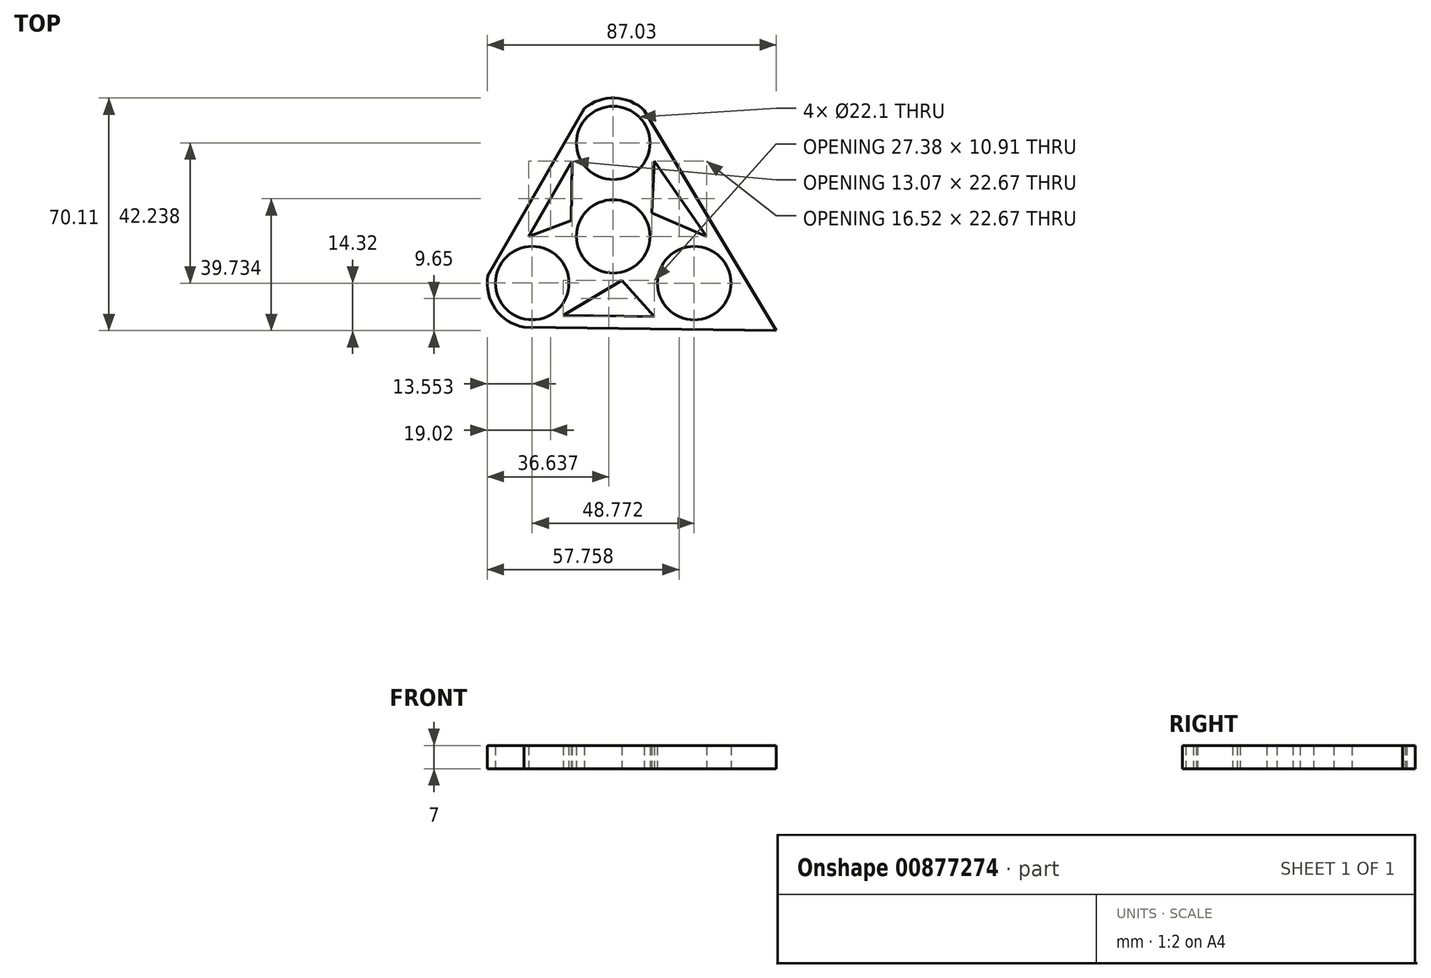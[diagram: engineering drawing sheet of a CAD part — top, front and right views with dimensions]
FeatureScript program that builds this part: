
annotation { "Feature Type Name" : "Feature", "Feature Type Description" : "" }
export const myFeature = defineFeature(function(context is Context, id is Id, definition is map)
    precondition{}
    {
        {
            var Q0;
            Q0=qCreatedBy(makeId("Top.planeOp"),FACE);
            var sketch = newSketch(context, id + "F0", { "sketchPlane" : qUnion([Q0])});
            skCircle(sketch, "E0", {"center": v(0, 0) * mm, "radius": 13.55 * mm});
            skCircle(sketch, "E1", {"center": v(0, 0) * mm, "radius": 11.05 * mm});
            skCircle(sketch, "E2", {"center": v(0, 28.16) * mm, "radius": 13.55 * mm});
            skCircle(sketch, "E3", {"center": v(0, 28.16) * mm, "radius": 11.05 * mm});
            skCircle(sketch, "E4.1.0", {"center": v(-24.39, -14.08) * mm, "radius": 11.05 * mm});
            skCircle(sketch, "E4.1.1", {"center": v(-24.39, -14.08) * mm, "radius": 13.55 * mm});
            skCircle(sketch, "E4.2.0", {"center": v(24.38, -14.08) * mm, "radius": 11.05 * mm});
            skCircle(sketch, "E4.2.1", {"center": v(24.38, -14.08) * mm, "radius": 13.55 * mm});
            skLineSegment(sketch, "E5", {"start": v(0, 0) * mm, "end": v(62.65, -36.25) * mm, "construction": true});
            skLineSegment(sketch, "E6", {"start": v(0, 0) * mm, "end": v(-56.78, -33.1) * mm, "construction": true});
            skLineSegment(sketch, "E7", {"start": v(0, 0) * mm, "end": v(0, 68.38) * mm, "construction": true});
            skLineSegment(sketch, "E8", {"start": v(0, 53.61) * mm, "end": v(49.09, -28.4) * mm});
            skLineSegment(sketch, "E9", {"start": v(49.09, -28.4) * mm, "end": v(-46.55, -27.14) * mm});
            skLineSegment(sketch, "E10", {"start": v(-46.55, -27.14) * mm, "end": v(0, 53.61) * mm});
            skLineSegment(sketch, "E11", {"start": v(12.39, 22.67) * mm, "end": v(28.08, 0) * mm});
            skLineSegment(sketch, "E12", {"start": v(28.08, 0) * mm, "end": v(11.56, 7.07) * mm});
            skLineSegment(sketch, "E13", {"start": v(11.56, 7.07) * mm, "end": v(12.39, 22.67) * mm});
            skLineSegment(sketch, "E14", {"start": v(-15, -23.84) * mm, "end": v(12.39, -24.2) * mm});
            skLineSegment(sketch, "E15", {"start": v(12.39, -24.2) * mm, "end": v(2.6, -13.3) * mm});
            skLineSegment(sketch, "E16", {"start": v(2.6, -13.3) * mm, "end": v(-15, -23.84) * mm});
            skLineSegment(sketch, "E17", {"start": v(-12.39, 22.67) * mm, "end": v(-25.45, 0) * mm});
            skLineSegment(sketch, "E18", {"start": v(-25.45, 0) * mm, "end": v(-12.66, 4.82) * mm});
            skLineSegment(sketch, "E19", {"start": v(-12.66, 4.82) * mm, "end": v(-12.39, 22.67) * mm});
            skSolve(sketch);
        }
        {
            var Q0;
            {var subQ5=sQuery(id+"F0.wireOp",EDGE,"E16");Q0=makeQuery(id+"F0.imprint","IMPRINT",FACE,{"disambiguationData":[TD([[makeQuery(id+"F0.imprint","IMPRINT",EDGE,{"derivedFrom":subQ5}),-1.0]])]});}
            var Q1;
            {var subQ0=sQuery(id+"F0.wireOp",EDGE,"E13");Q1=makeQuery(id+"F0.imprint","IMPRINT",FACE,{"disambiguationData":[TD([[makeQuery(id+"F0.imprint","IMPRINT",EDGE,{"derivedFrom":subQ0}),1.0]])]});}
            var Q2;
            Q2=makeQuery(id+"F0.imprint","IMPRINT",FACE,{"disambiguationData":[TD([[makeQuery(id+"F0.imprint","IMPRINT",EDGE,{"derivedFrom":sQuery(id+"F0.wireOp",EDGE,"E3")}),-1.0]])]});
            var Q3;
            Q3=makeQuery(id+"F0.imprint","IMPRINT",FACE,{"disambiguationData":[TD([[makeQuery(id+"F0.imprint","IMPRINT",EDGE,{"derivedFrom":sQuery(id+"F0.wireOp",EDGE,"E1")}),-1.0]])]});
            var Q4;
            Q4=makeQuery(id+"F0.imprint","IMPRINT",FACE,{"disambiguationData":[TD([[makeQuery(id+"F0.imprint","IMPRINT",EDGE,{"derivedFrom":sQuery(id+"F0.wireOp",EDGE,"E4.2.1")}),-1.0]])]});
            var Q5;
            Q5=makeQuery(id+"F0.imprint","IMPRINT",FACE,{"disambiguationData":[TD([[makeQuery(id+"F0.imprint","IMPRINT",EDGE,{"derivedFrom":sQuery(id+"F0.wireOp",EDGE,"E4.2.0")}),-1.0]])]});
            var Q6;
            Q6=makeQuery(id+"F0.imprint","IMPRINT",FACE,{"disambiguationData":[TD([[makeQuery(id+"F0.imprint","IMPRINT",EDGE,{"derivedFrom":sQuery(id+"F0.wireOp",EDGE,"E4.1.0")}),-1.0]])]});
            var Q7;
            {var subQ0=sQuery(id+"F0.wireOp",EDGE,"E10");var subQ1=sQuery(id+"F0.wireOp",EDGE,"E4.1.1");var subQ2=makeQuery(id+"F0.imprint","INTERSECT",VERTEX,{"disambiguationData":[OD(0.0)],"derivedFrom":[subQ1,subQ0]});Q7=makeQuery(id+"F0.imprint","IMPRINT",FACE,{"disambiguationData":[TD([[makeQuery(id+"F0.imprint","IMPRINT",EDGE,{"disambiguationData":[TD([[subQ2,-1.0]])],"derivedFrom":subQ1}),-1.0]])]});}
            var Q8;
            {var subQ0=sQuery(id+"F0.wireOp",EDGE,"E8");var subQ1=sQuery(id+"F0.wireOp",EDGE,"E2");var subQ2=makeQuery(id+"F0.imprint","INTERSECT",VERTEX,{"disambiguationData":[OD(0.0)],"derivedFrom":[subQ1,subQ0]});Q8=makeQuery(id+"F0.imprint","IMPRINT",FACE,{"disambiguationData":[TD([[makeQuery(id+"F0.imprint","IMPRINT",EDGE,{"disambiguationData":[TD([[subQ2,-1.0]])],"derivedFrom":subQ1}),-1.0]])]});}
            extrude(context, id + "F1", {"entities" : qUnion([Q0, Q1, Q2, Q3, Q4, Q5, Q6, Q7, Q8]), "depth" : 7 * mm, "offsetDistance" : 25 * mm});
        }
    });
